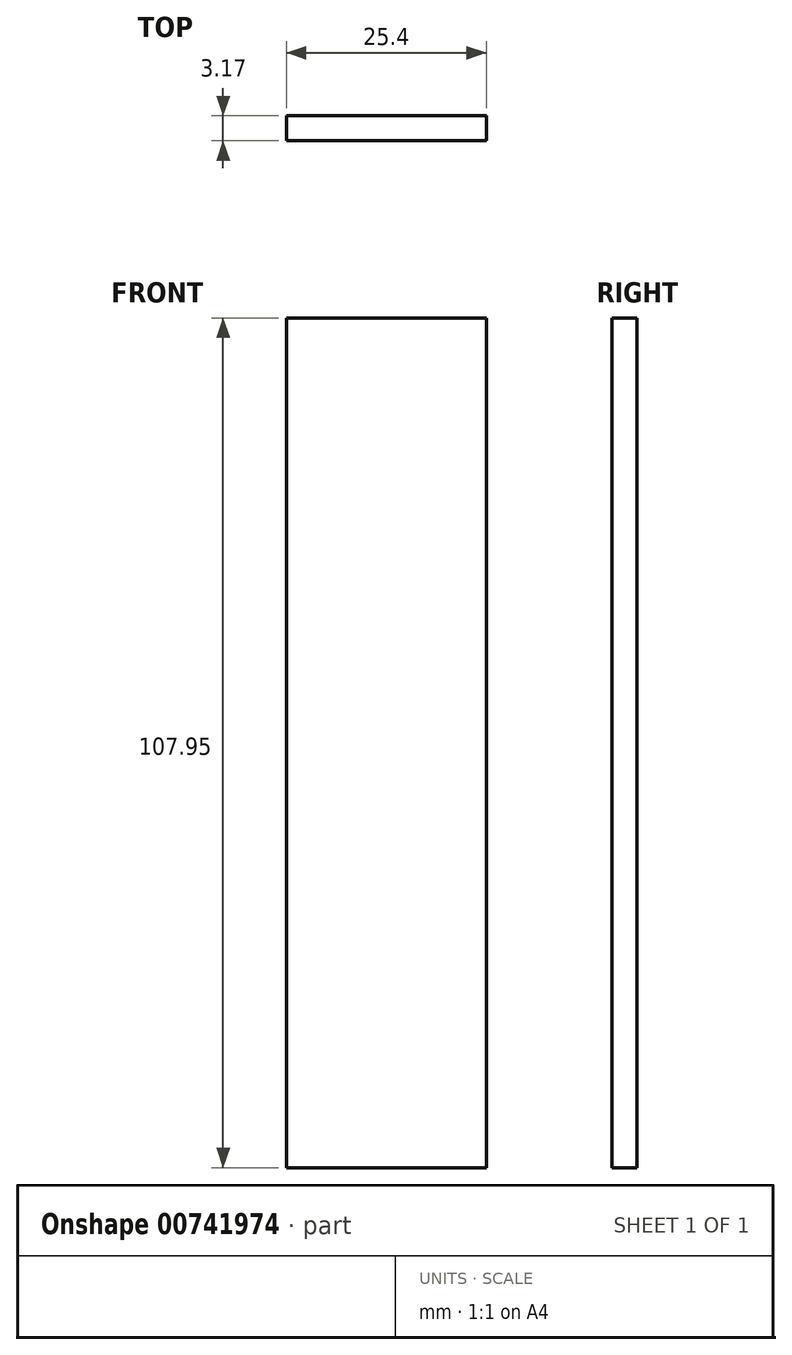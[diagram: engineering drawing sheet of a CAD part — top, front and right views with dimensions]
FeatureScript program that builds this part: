
annotation { "Feature Type Name" : "Feature", "Feature Type Description" : "" }
export const myFeature = defineFeature(function(context is Context, id is Id, definition is map)
    precondition{}
    {
        {
            var Q0;
            Q0=qCreatedBy(makeId("Front.planeOp"),FACE);
            var sketch = newSketch(context, id + "F0", { "sketchPlane" : qUnion([Q0])});
            skLineSegment(sketch, "E0.bottom", {"start": v(6.46, 57.38) * mm, "end": v(31.86, 57.38) * mm});
            skLineSegment(sketch, "E0.top", {"start": v(6.46, -50.57) * mm, "end": v(31.86, -50.57) * mm});
            skLineSegment(sketch, "E0.left", {"start": v(6.46, 57.38) * mm, "end": v(6.46, -50.57) * mm});
            skLineSegment(sketch, "E0.right", {"start": v(31.86, 57.38) * mm, "end": v(31.86, -50.57) * mm});
            skSolve(sketch);
        }
        {
            var Q0;
            Q0 = qSketchRegion(id + "F0", true);
            extrude(context, id + "F1", {"entities" : qUnion([Q0]), "depth" : 3.17 * mm, "offsetDistance" : 25.4 * mm});
        }
    });
